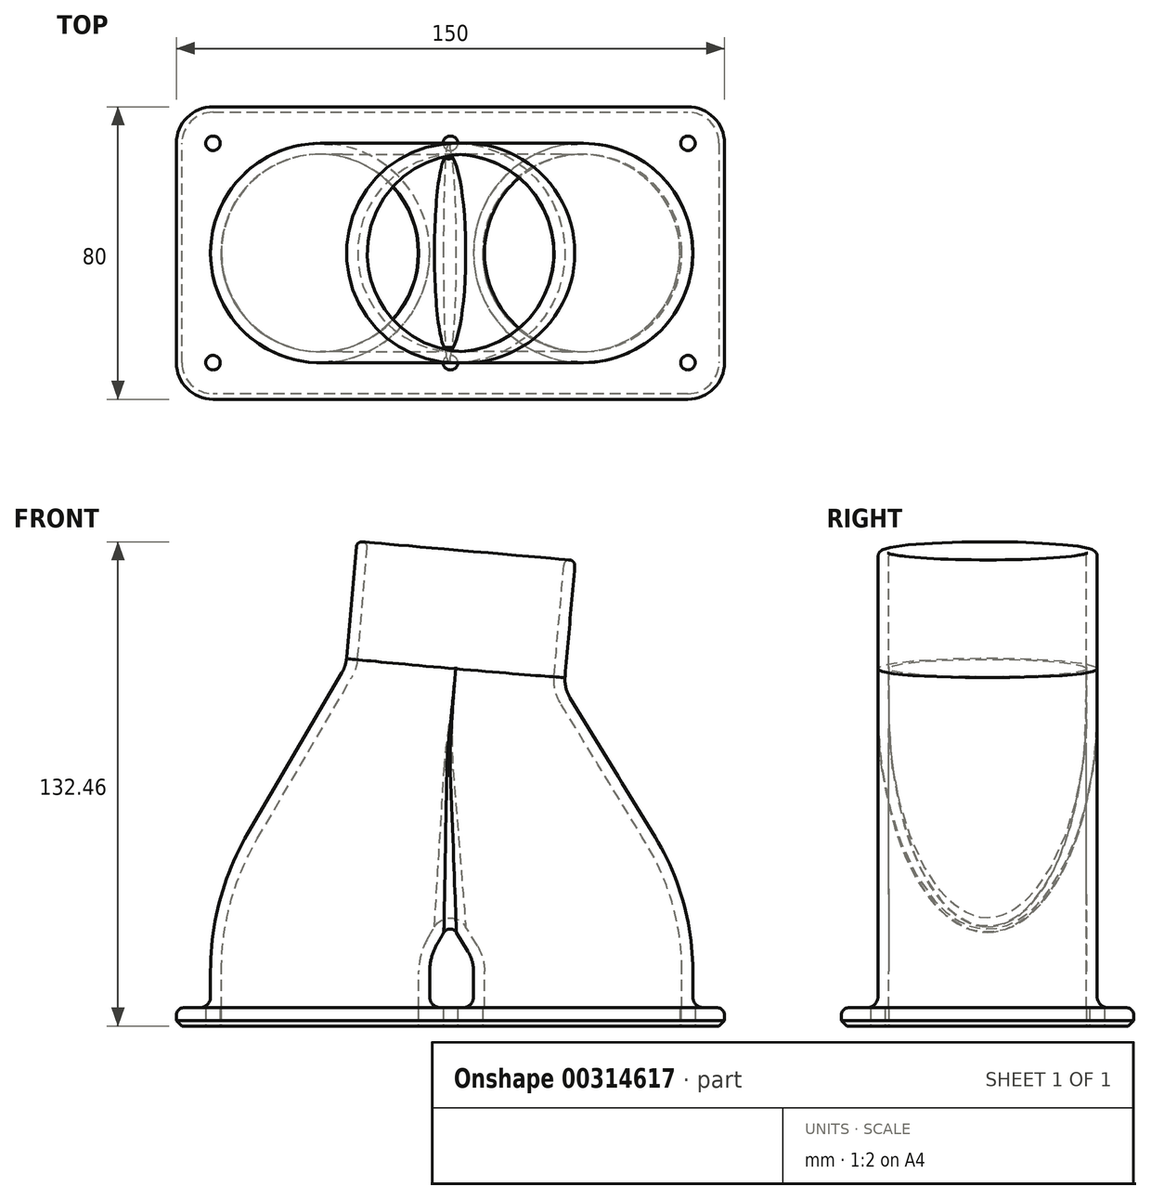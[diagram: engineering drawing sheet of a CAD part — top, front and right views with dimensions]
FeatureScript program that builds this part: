
annotation { "Feature Type Name" : "Feature", "Feature Type Description" : "" }
export const myFeature = defineFeature(function(context is Context, id is Id, definition is map)
    precondition{}
    {
        {
            var Q0;
            Q0=qCreatedBy(makeId("Front.planeOp"),FACE);
            var sketch = newSketch(context, id + "F0", { "sketchPlane" : qUnion([Q0])});
            skLineSegment(sketch, "E0", {"start": v(0, 0) * mm, "end": v(0, 170) * mm, "construction": true});
            skLineSegment(sketch, "E1", {"start": v(0, 85) * mm, "end": v(8.37, 180.61) * mm, "construction": true});
            skLineSegment(sketch, "E2", {"start": v(36, 0) * mm, "end": v(36, 15) * mm});
            skLineSegment(sketch, "E3", {"start": v(30.14, 35.85) * mm, "end": v(6.87, 73.94) * mm});
            skLineSegment(sketch, "E4", {"start": v(1.16, 98.28) * mm, "end": v(3.94, 130) * mm});
            skLineSegment(sketch, "E5", {"start": v(3.94, 130) * mm, "end": v(56.9, 125.37) * mm, "construction": true});
            skLineSegment(sketch, "E6", {"start": v(0.01, 85.17) * mm, "end": v(52.83, 80.55) * mm, "construction": true});
            skPoint(sketch, "E7.visualSharp", {"position": v(0.01, 85.17) * mm});
            skArc(sketch, "E7.filletArc", {"start": v(1.16, 98.28) * mm, "mid": v(2.07, 85.65) * mm, "end": v(6.87, 73.94) * mm});
            skPoint(sketch, "E8.visualSharp", {"position": v(36, 26.25) * mm});
            skArc(sketch, "E8.filletArc", {"start": v(36, 15) * mm, "mid": v(34.5, 25.83) * mm, "end": v(30.14, 35.85) * mm});
            skLineSegment(sketch, "E9", {"start": v(-36, 0) * mm, "end": v(-36, 15) * mm});
            skArc(sketch, "E10.MirrorCS", {"start": v(1.16, 98.28) * mm, "mid": v(-0.58, 89.62) * mm, "end": v(-4.17, 81.55) * mm});
            skLineSegment(sketch, "E11", {"start": v(-29.83, 37.74) * mm, "end": v(-4.17, 81.55) * mm});
            skPoint(sketch, "E12.visualSharp", {"position": v(-36, 27.2) * mm});
            skArc(sketch, "E12.filletArc", {"start": v(-29.83, 37.74) * mm, "mid": v(-34.43, 26.78) * mm, "end": v(-36, 15) * mm});
            skPoint(sketch, "E13.orphan", {"position": v(-8.69, 75.3) * mm});
            skSolve(sketch);
        }
        {
            var Q0;
            Q0=qCreatedBy(makeId("Top.planeOp"),FACE);
            var sketch = newSketch(context, id + "F1", { "sketchPlane" : qUnion([Q0])});
            skCircle(sketch, "E14", {"center": v(36.32, 0) * mm, "radius": 30 * mm});
            skCircle(sketch, "E15", {"center": v(-35.67, 0) * mm, "radius": 30 * mm});
            skSolve(sketch);
        }
        {
            var Q0;
            Q0=makeQuery(id+"F1.imprint","IMPRINT",FACE,{"disambiguationData":[TD([[makeQuery(id+"F1.imprint","IMPRINT",EDGE,{"derivedFrom":sQuery(id+"F1.wireOp",EDGE,"E14")}),1.0]])]});
            var Q1;
            Q1=sQuery(id+"F0.wireOp",EDGE,"E2");
            var Q2;
            Q2=sQuery(id+"F0.wireOp",EDGE,"E8.filletArc");
            var Q3;
            Q3=sQuery(id+"F0.wireOp",EDGE,"E3");
            var Q4;
            Q4=sQuery(id+"F0.wireOp",EDGE,"E7.filletArc");
            var Q5;
            Q5=sQuery(id+"F0.wireOp",EDGE,"E4");
            sweep(context, id + "F2", {"profiles" : qUnion([Q0]), "path" : qUnion([Q1, Q2, Q3, Q4, Q5])});
        }
        {
            var Q0;
            Q0=makeQuery(id+"F1.imprint","IMPRINT",FACE,{"disambiguationData":[TD([[makeQuery(id+"F1.imprint","IMPRINT",EDGE,{"derivedFrom":sQuery(id+"F1.wireOp",EDGE,"E15")}),1.0]])]});
            var Q1;
            Q1=sQuery(id+"F0.wireOp",EDGE,"E9");
            var Q2;
            Q2=sQuery(id+"F0.wireOp",EDGE,"E12.filletArc");
            var Q3;
            Q3=sQuery(id+"F0.wireOp",EDGE,"E11");
            var Q4;
            Q4=sQuery(id+"F0.wireOp",EDGE,"E10.MirrorCS");
            var Q5;
            Q5=sQuery(id+"F0.wireOp",EDGE,"E4");
            sweep(context, id + "F3", {"profiles" : qUnion([Q0]), "path" : qUnion([Q1, Q2, Q3, Q4, Q5])});
        }
        {
            var Q0;
            Q0=makeQuery(id+"F3.opSweep","SWEPT_BODY",BODY,{"disambiguationData":[OSD([sQuery(id+"F0.wireOp",EDGE,"E4"),sQuery(id+"F1.wireOp",EDGE,"E15")])]});
            var Q1;
            Q1=makeQuery(id+"F2.opSweep","SWEPT_BODY",BODY,{"disambiguationData":[OSD([sQuery(id+"F0.wireOp",EDGE,"E4"),sQuery(id+"F1.wireOp",EDGE,"E14")])]});
            booleanBodies(context, id + "F4", {"operationType" : BooleanOperationType.UNION, "tools" : qUnion([Q0, Q1])});
        }
        {
            var Q0;
            Q0=makeQuery(id+"F4.opBoolean","INTERSECT",EDGE,{"derivedFrom":[makeQuery(id+"F2.opSweep","SWEPT_FACE",FACE,{"disambiguationData":[OSD([sQuery(id+"F0.wireOp",EDGE,"E3"),sQuery(id+"F1.wireOp",EDGE,"E14")])]}),makeQuery(id+"F3.opSweep","SWEPT_FACE",FACE,{"disambiguationData":[OSD([sQuery(id+"F0.wireOp",EDGE,"E11"),sQuery(id+"F1.wireOp",EDGE,"E15")])]})]});
            fillet(context, id + "F5", {"entities" : qUnion([Q0]), "radius" : 2 * mm, "tangentPropagation" : true, "allowEdgeOverflow" : false});
        }
        {
            var Q0;
            {var subQ0=sQuery(id+"F0.wireOp",VERTEX,"E4.end");Q0=makeQuery(id+"F4.opBoolean","MERGE",FACE,{"derivedFrom":[makeQuery(id+"F2.opSweep","CAP_FACE",FACE,{"disambiguationData":[OSD([subQ0,sQuery(id+"F1.wireOp",EDGE,"E14")])],"isStart":false}),makeQuery(id+"F3.opSweep","CAP_FACE",FACE,{"disambiguationData":[OSD([subQ0,sQuery(id+"F1.wireOp",EDGE,"E15")])],"isStart":false})]});}
            var Q1;
            Q1=makeQuery(id+"F2.opSweep","CAP_FACE",FACE,{"disambiguationData":[OSD([sQuery(id+"F0.wireOp",VERTEX,"E2.start"),sQuery(id+"F1.wireOp",EDGE,"E14")])],"isStart":true});
            var Q2;
            Q2=makeQuery(id+"F3.opSweep","CAP_FACE",FACE,{"disambiguationData":[OSD([sQuery(id+"F0.wireOp",VERTEX,"E9.start"),sQuery(id+"F1.wireOp",EDGE,"E15")])],"isStart":true});
            shell(context, id + "F6", {"entities" : qUnion([Q0, Q1, Q2]), "thickness" : 3 * mm});
        }
        {
            var Q0;
            Q0=qCreatedBy(makeId("Top.planeOp"),FACE);
            var sketch = newSketch(context, id + "F7", { "sketchPlane" : qUnion([Q0])});
            skLineSegment(sketch, "E16.bottom", {"start": v(-75, 40) * mm, "end": v(75, 40) * mm});
            skLineSegment(sketch, "E16.top", {"start": v(-75, -40) * mm, "end": v(75, -40) * mm});
            skLineSegment(sketch, "E16.left", {"start": v(-75, 40) * mm, "end": v(-75, -40) * mm});
            skLineSegment(sketch, "E16.right", {"start": v(75, 40) * mm, "end": v(75, -40) * mm});
            skPoint(sketch, "E17", {"position": v(-65, -30) * mm});
            skPoint(sketch, "E18", {"position": v(-65, 30) * mm});
            skPoint(sketch, "E19", {"position": v(65, 30) * mm});
            skPoint(sketch, "E20", {"position": v(65, -30) * mm});
            skPoint(sketch, "E21", {"position": v(0, 30) * mm});
            skPoint(sketch, "E22", {"position": v(0, -30) * mm});
            skSolve(sketch);
        }
        {
            var Q0;
            Q0=makeQuery(id+"F7.imprint","IMPRINT",FACE,{"disambiguationData":[TD([[makeQuery(id+"F7.imprint","IMPRINT",EDGE,{"derivedFrom":sQuery(id+"F7.wireOp",EDGE,"E16.bottom")}),-1.0]])]});
            var Q1;
            Q1=sQuery(id+"F1.wireOp",EDGE,"E14");
            var Q2;
            Q2=sQuery(id+"F1.wireOp",EDGE,"E15");
            var Q3;
            Q3=sQuery(id+"F7.wireOp",EDGE,"E16.top");
            var Q4;
            Q4=sQuery(id+"F7.wireOp",EDGE,"E16.right");
            var Q5;
            Q5=sQuery(id+"F7.wireOp",EDGE,"E16.bottom");
            var Q6;
            Q6=sQuery(id+"F7.wireOp",EDGE,"E16.left");
            extrude(context, id + "F8", {"entities" : qUnion([Q0]), "operationType" : NewBodyOperationType.ADD, "surfaceEntities" : qUnion([Q1, Q2, Q3, Q4, Q5, Q6]), "depth" : 5 * mm});
        }
        {
            var Q0;
            Q0=makeQuery(id+"F8.boolean.opBoolean","MERGE",FACE,{"derivedFrom":[makeQuery(id+"F2.opSweep","CAP_FACE",FACE,{"disambiguationData":[OSD([sQuery(id+"F0.wireOp",VERTEX,"E2.start"),sQuery(id+"F1.wireOp",EDGE,"E14")])],"isStart":true}),makeQuery(id+"F3.opSweep","CAP_FACE",FACE,{"disambiguationData":[OSD([sQuery(id+"F0.wireOp",VERTEX,"E9.start"),sQuery(id+"F1.wireOp",EDGE,"E15")])],"isStart":true}),makeQuery(id+"F8.opExtrude","CAP_FACE",FACE,{"disambiguationData":[OSD([sQuery(id+"F7.wireOp",EDGE,"E16.bottom"),sQuery(id+"F7.wireOp",EDGE,"E16.top"),sQuery(id+"F7.wireOp",EDGE,"E16.left"),sQuery(id+"F7.wireOp",EDGE,"E16.right")])],"isStart":true})]});
            var sketch = newSketch(context, id + "F9", { "sketchPlane" : qUnion([Q0])});
            skCircle(sketch, "E23", {"center": v(-35.8, 0) * mm, "radius": 27 * mm});
            skCircle(sketch, "E24", {"center": v(35.8, 0) * mm, "radius": 27 * mm});
            skSolve(sketch);
        }
        {
            var Q0;
            Q0=makeQuery(id+"F9.imprint","IMPRINT",FACE,{"disambiguationData":[TD([[makeQuery(id+"F9.imprint","IMPRINT",EDGE,{"derivedFrom":sQuery(id+"F9.wireOp",EDGE,"E23")}),1.0]])]});
            var Q1;
            Q1=makeQuery(id+"F9.imprint","IMPRINT",FACE,{"disambiguationData":[TD([[makeQuery(id+"F9.imprint","IMPRINT",EDGE,{"derivedFrom":sQuery(id+"F9.wireOp",EDGE,"E24")}),1.0]])]});
            var Q2;
            Q2=sQuery(id+"F9.wireOp",EDGE,"E23");
            var Q3;
            Q3=sQuery(id+"F9.wireOp",EDGE,"E24");
            extrude(context, id + "F10", {"entities" : qUnion([Q0, Q1]), "operationType" : NewBodyOperationType.REMOVE, "surfaceEntities" : qUnion([Q2, Q3]), "oppositeDirection" : true, "depth" : 5 * mm});
        }
        {
            var Q0;
            Q0=sQuery(id+"F7.wireOp",VERTEX,"E17");
            var Q1;
            Q1=sQuery(id+"F7.wireOp",VERTEX,"E22");
            var Q2;
            Q2=sQuery(id+"F7.wireOp",VERTEX,"E19");
            var Q3;
            Q3=sQuery(id+"F7.wireOp",VERTEX,"E18");
            var Q4;
            Q4=sQuery(id+"F7.wireOp",VERTEX,"E21");
            var Q5;
            Q5=sQuery(id+"F7.wireOp",VERTEX,"E20");
            var Q6;
            Q6=makeQuery(id+"F3.opSweep","SWEPT_BODY",BODY,{"disambiguationData":[OSD([sQuery(id+"F0.wireOp",EDGE,"E4"),sQuery(id+"F1.wireOp",EDGE,"E15")])]});
            hole(context, id + "F11", {"style" : HoleStyle.SIMPLE, "endStyle" : HoleEndStyle.BLIND, "oppositeDirection" : true, "holeDiameter" : 4 * mm, "holeDepth" : 5 * mm, "tappedDepth" : 12 * mm, "tapClearance" : 3, "startFromSketch" : true, "locations" : qUnion([Q0, Q1, Q2, Q3, Q4, Q5]), "scope" : qUnion([Q6])});
        }
        {
            var Q0;
            Q0=makeQuery(id+"F8.boolean.opBoolean","INTERSECT",EDGE,{"derivedFrom":[makeQuery(id+"F3.opSweep","SWEPT_FACE",FACE,{"disambiguationData":[OSD([sQuery(id+"F0.wireOp",EDGE,"E9"),sQuery(id+"F1.wireOp",EDGE,"E15")])]}),makeQuery(id+"F8.opExtrude","CAP_FACE",FACE,{"disambiguationData":[OSD([sQuery(id+"F7.wireOp",EDGE,"E16.bottom"),sQuery(id+"F7.wireOp",EDGE,"E16.top"),sQuery(id+"F7.wireOp",EDGE,"E16.left"),sQuery(id+"F7.wireOp",EDGE,"E16.right")])],"isStart":false})]});
            var Q1;
            Q1=makeQuery(id+"F8.boolean.opBoolean","INTERSECT",EDGE,{"derivedFrom":[makeQuery(id+"F2.opSweep","SWEPT_FACE",FACE,{"disambiguationData":[OSD([sQuery(id+"F0.wireOp",EDGE,"E2"),sQuery(id+"F1.wireOp",EDGE,"E14")])]}),makeQuery(id+"F8.opExtrude","CAP_FACE",FACE,{"disambiguationData":[OSD([sQuery(id+"F7.wireOp",EDGE,"E16.bottom"),sQuery(id+"F7.wireOp",EDGE,"E16.top"),sQuery(id+"F7.wireOp",EDGE,"E16.left"),sQuery(id+"F7.wireOp",EDGE,"E16.right")])],"isStart":false})]});
            fillet(context, id + "F12", {"entities" : qUnion([Q0, Q1]), "radius" : 3 * mm, "tangentPropagation" : true, "allowEdgeOverflow" : false});
        }
        {
            var Q0;
            Q0=makeQuery(id+"F8.opExtrude","SWEPT_EDGE",EDGE,{"disambiguationData":[OSD([sQuery(id+"F7.wireOp",EDGE,"E16.top"),sQuery(id+"F7.wireOp",EDGE,"E16.left")])]});
            var Q1;
            Q1=makeQuery(id+"F8.opExtrude","SWEPT_EDGE",EDGE,{"disambiguationData":[OSD([sQuery(id+"F7.wireOp",EDGE,"E16.top"),sQuery(id+"F7.wireOp",EDGE,"E16.right")])]});
            var Q2;
            Q2=makeQuery(id+"F8.opExtrude","SWEPT_EDGE",EDGE,{"disambiguationData":[OSD([sQuery(id+"F7.wireOp",EDGE,"E16.bottom"),sQuery(id+"F7.wireOp",EDGE,"E16.right")])]});
            var Q3;
            Q3=makeQuery(id+"F8.opExtrude","SWEPT_EDGE",EDGE,{"disambiguationData":[OSD([sQuery(id+"F7.wireOp",EDGE,"E16.bottom"),sQuery(id+"F7.wireOp",EDGE,"E16.left")])]});
            fillet(context, id + "F13", {"entities" : qUnion([Q0, Q1, Q2, Q3]), "radius" : 10 * mm, "tangentPropagation" : true, "allowEdgeOverflow" : false});
        }
        {
            var Q0;
            {var subQ0=sQuery(id+"F7.wireOp",EDGE,"E16.top");var subQ1=sQuery(id+"F7.wireOp",EDGE,"E16.bottom");var subQ2=sQuery(id+"F7.wireOp",EDGE,"E16.left");var subQ3=sQuery(id+"F7.wireOp",EDGE,"E16.right");Q0=makeQuery(id+"F13.opFillet","BLEND_EDGE",EDGE,{"blendedFrom":[makeQuery(id+"F8.opExtrude","SWEPT_EDGE",EDGE,{"disambiguationData":[OSD([subQ0,subQ2])]}),makeQuery(id+"F8.boolean.opBoolean","SPLIT",FACE,{"disambiguationData":[TD([makeQuery(id+"F8.opExtrude","SWEPT_FACE",FACE,{"disambiguationData":[OSD([subQ1])]})])],"derivedFrom":makeQuery(id+"F8.opExtrude","CAP_FACE",FACE,{"disambiguationData":[OSD([subQ1,subQ0,subQ2,subQ3])],"isStart":false})})],"blendedInto":[makeQuery(id+"F8.boolean.opBoolean","SPLIT",FACE,{"disambiguationData":[TD([makeQuery(id+"F8.opExtrude","SWEPT_FACE",FACE,{"disambiguationData":[OSD([subQ1])]})])],"derivedFrom":makeQuery(id+"F8.opExtrude","CAP_FACE",FACE,{"disambiguationData":[OSD([subQ1,subQ0,subQ2,subQ3])],"isStart":false})})]});}
            var Q1;
            Q1=makeQuery(id+"F8.opExtrude","CAP_EDGE",EDGE,{"disambiguationData":[OSD([sQuery(id+"F7.wireOp",EDGE,"E16.left")])],"isStart":false});
            fillet(context, id + "F14", {"entities" : qUnion([Q0, Q1]), "radius" : 2 * mm, "tangentPropagation" : true, "allowEdgeOverflow" : false});
        }
        {
            var Q0;
            Q0=makeQuery(id+"F10.boolean.opBoolean","COPY",EDGE,{"derivedFrom":makeQuery(id+"F10.opExtrude","CAP_EDGE",EDGE,{"disambiguationData":[OSD([sQuery(id+"F9.wireOp",EDGE,"E23")])],"isStart":true})});
            var Q1;
            Q1=makeQuery(id+"F10.boolean.opBoolean","COPY",EDGE,{"derivedFrom":makeQuery(id+"F10.opExtrude","CAP_EDGE",EDGE,{"disambiguationData":[OSD([sQuery(id+"F9.wireOp",EDGE,"E24")])],"isStart":true})});
            var Q2;
            Q2=makeQuery(id+"F8.opExtrude","CAP_EDGE",EDGE,{"disambiguationData":[OSD([sQuery(id+"F7.wireOp",EDGE,"E16.top")])],"isStart":true});
            var Q3;
            {var subQ0=sQuery(id+"F7.wireOp",EDGE,"E16.right");var subQ1=sQuery(id+"F7.wireOp",EDGE,"E16.top");Q3=makeQuery(id+"F13.opFillet","BLEND_EDGE",EDGE,{"blendedFrom":[makeQuery(id+"F8.opExtrude","SWEPT_EDGE",EDGE,{"disambiguationData":[OSD([subQ1,subQ0])]}),makeQuery(id+"F8.boolean.opBoolean","MERGE",FACE,{"derivedFrom":[makeQuery(id+"F2.opSweep","CAP_FACE",FACE,{"disambiguationData":[OSD([sQuery(id+"F0.wireOp",VERTEX,"E2.start"),sQuery(id+"F1.wireOp",EDGE,"E14")])],"isStart":true}),makeQuery(id+"F3.opSweep","CAP_FACE",FACE,{"disambiguationData":[OSD([sQuery(id+"F0.wireOp",VERTEX,"E9.start"),sQuery(id+"F1.wireOp",EDGE,"E15")])],"isStart":true}),makeQuery(id+"F8.opExtrude","CAP_FACE",FACE,{"disambiguationData":[OSD([sQuery(id+"F7.wireOp",EDGE,"E16.bottom"),subQ1,sQuery(id+"F7.wireOp",EDGE,"E16.left"),subQ0])],"isStart":true})]})],"blendedInto":[makeQuery(id+"F8.boolean.opBoolean","MERGE",FACE,{"derivedFrom":[makeQuery(id+"F2.opSweep","CAP_FACE",FACE,{"disambiguationData":[OSD([sQuery(id+"F0.wireOp",VERTEX,"E2.start"),sQuery(id+"F1.wireOp",EDGE,"E14")])],"isStart":true}),makeQuery(id+"F3.opSweep","CAP_FACE",FACE,{"disambiguationData":[OSD([sQuery(id+"F0.wireOp",VERTEX,"E9.start"),sQuery(id+"F1.wireOp",EDGE,"E15")])],"isStart":true}),makeQuery(id+"F8.opExtrude","CAP_FACE",FACE,{"disambiguationData":[OSD([sQuery(id+"F7.wireOp",EDGE,"E16.bottom"),subQ1,sQuery(id+"F7.wireOp",EDGE,"E16.left"),subQ0])],"isStart":true})]})]});}
            chamfer(context, id + "F15", {"entities" : qUnion([Q0, Q1, Q2, Q3]), "width" : 1.5 * mm, "tangentPropagation" : true});
        }
        {
            var Q0;
            Q0=makeQuery(id+"F3.opSweep","CAP_EDGE",EDGE,{"disambiguationData":[OSD([sQuery(id+"F0.wireOp",VERTEX,"E4.end"),sQuery(id+"F1.wireOp",EDGE,"E15")])],"isStart":false});
            var Q1;
            Q1=makeQuery(id+"F6.opShell","OFFSET_EDGE",EDGE,{"disambiguationData":[OSD([sQuery(id+"F0.wireOp",VERTEX,"E4.end"),sQuery(id+"F1.wireOp",EDGE,"E15")])]});
            fillet(context, id + "F16", {"entities" : qUnion([Q0, Q1]), "radius" : 1.5 * mm, "tangentPropagation" : true, "allowEdgeOverflow" : false});
        }
    });
